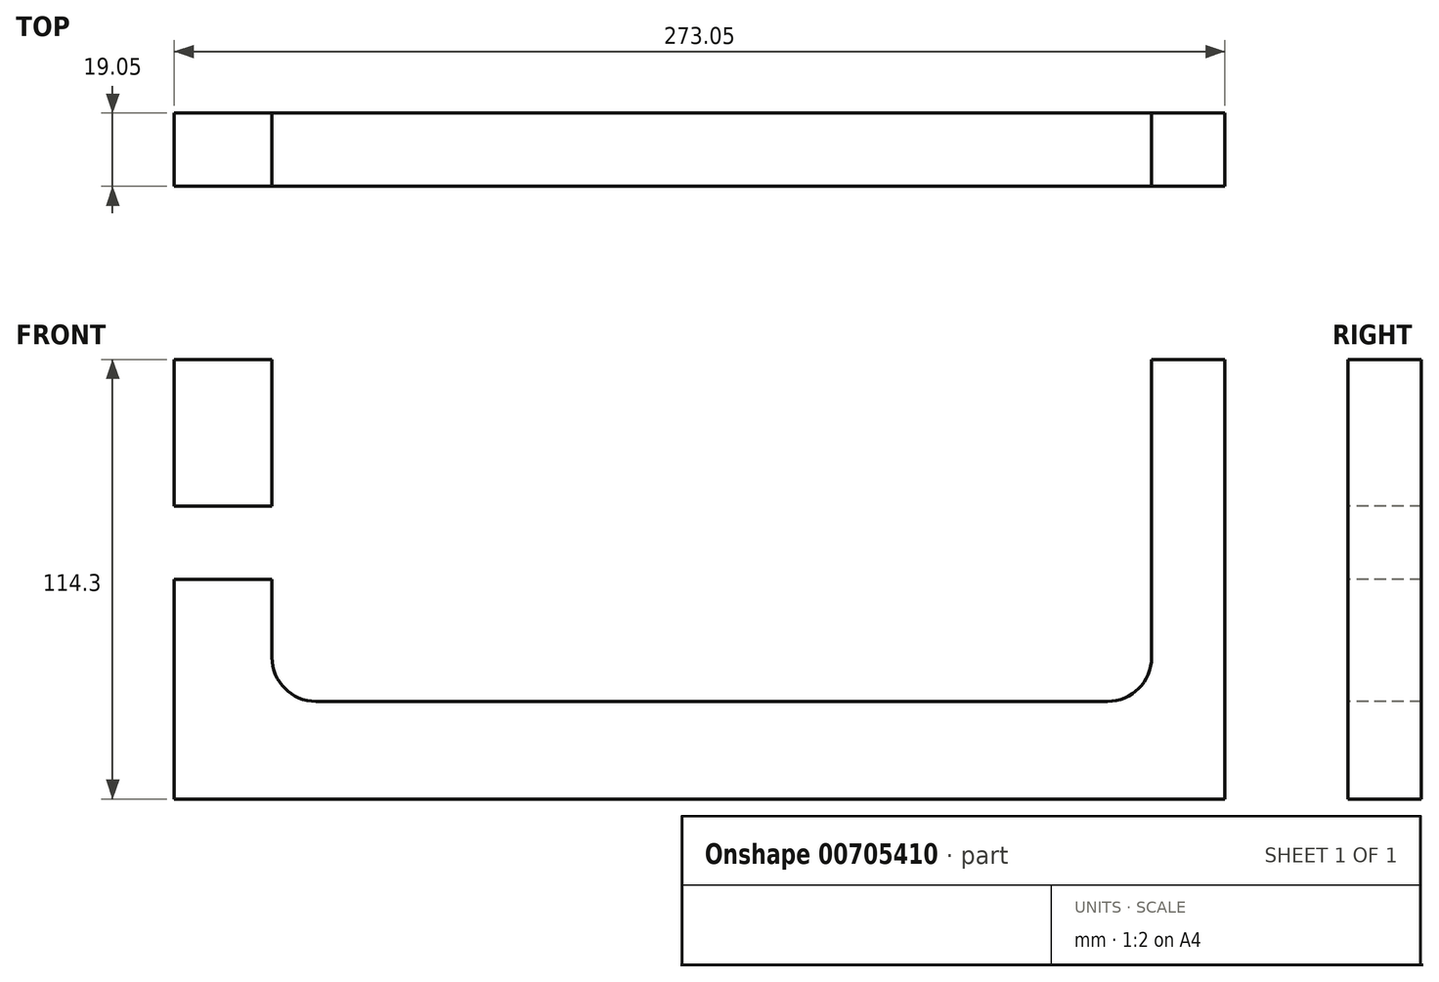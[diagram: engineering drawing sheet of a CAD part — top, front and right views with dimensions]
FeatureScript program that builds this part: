
annotation { "Feature Type Name" : "Feature", "Feature Type Description" : "" }
export const myFeature = defineFeature(function(context is Context, id is Id, definition is map)
    precondition{}
    {
        {
            var Q0;
            Q0=qCreatedBy(makeId("Front.planeOp"),FACE);
            var sketch = newSketch(context, id + "F0", { "sketchPlane" : qUnion([Q0])});
            skLineSegment(sketch, "E0.bottom", {"start": v(0, 0) * mm, "end": v(273.05, 0) * mm});
            skLineSegment(sketch, "E0.top", {"start": v(0, 114.3) * mm, "end": v(273.05, 114.3) * mm});
            skLineSegment(sketch, "E0.left", {"start": v(0, 0) * mm, "end": v(0, 114.3) * mm});
            skLineSegment(sketch, "E0.right", {"start": v(273.05, 0) * mm, "end": v(273.05, 114.3) * mm});
            skSolve(sketch);
        }
        {
            var Q0;
            Q0 = qSketchRegion(id + "F0", true);
            extrude(context, id + "F1", {"entities" : qUnion([Q0]), "depth" : 19.05 * mm, "offsetDistance" : 25.4 * mm});
        }
        {
            var Q0;
            Q0=makeQuery(id+"F1.opExtrude","CAP_FACE",FACE,{"disambiguationData":[OSD([sQuery(id+"F0.wireOp",EDGE,"E0.bottom"),sQuery(id+"F0.wireOp",EDGE,"E0.top"),sQuery(id+"F0.wireOp",EDGE,"E0.left"),sQuery(id+"F0.wireOp",EDGE,"E0.right")])],"isStart":false});
            var sketch = newSketch(context, id + "F2", { "sketchPlane" : qUnion([Q0])});
            skLineSegment(sketch, "E1.bottom", {"start": v(0, 76.2) * mm, "end": v(25.4, 76.2) * mm});
            skLineSegment(sketch, "E1.top", {"start": v(0, 57.15) * mm, "end": v(25.4, 57.15) * mm});
            skLineSegment(sketch, "E1.left", {"start": v(0, 76.2) * mm, "end": v(0, 57.15) * mm});
            skLineSegment(sketch, "E1.right", {"start": v(25.4, 76.2) * mm, "end": v(25.4, 57.15) * mm});
            skLineSegment(sketch, "E2.bottom", {"start": v(25.4, 114.3) * mm, "end": v(254, 114.3) * mm});
            skLineSegment(sketch, "E2.top", {"start": v(36.83, 25.4) * mm, "end": v(242.57, 25.4) * mm});
            skLineSegment(sketch, "E2.left", {"start": v(25.4, 114.3) * mm, "end": v(25.4, 36.83) * mm});
            skLineSegment(sketch, "E2.right", {"start": v(254, 114.3) * mm, "end": v(254, 36.83) * mm});
            skPoint(sketch, "E3.visualSharp", {"position": v(25.4, 25.4) * mm});
            skArc(sketch, "E3.filletArc", {"start": v(25.4, 36.83) * mm, "mid": v(28.75, 28.75) * mm, "end": v(36.83, 25.4) * mm});
            skPoint(sketch, "E4.visualSharp", {"position": v(254, 25.4) * mm});
            skArc(sketch, "E4.filletArc", {"start": v(242.57, 25.4) * mm, "mid": v(250.65, 28.75) * mm, "end": v(254, 36.83) * mm});
            skSolve(sketch);
        }
        {
            var Q0;
            Q0 = qSketchRegion(id + "F2", true);
            extrude(context, id + "F3", {"entities" : qUnion([Q0]), "operationType" : NewBodyOperationType.REMOVE, "oppositeDirection" : true, "depth" : 25.4 * mm, "offsetDistance" : 25.4 * mm});
        }
    });
